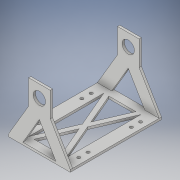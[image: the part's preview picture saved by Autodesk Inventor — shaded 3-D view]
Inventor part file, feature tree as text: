
AUTODESK INVENTOR PART (.ipt)
format: ipt  version: 2019 (Build 230136000, 136)  size: 211,968 bytes
history: native  units: in
note: dims shown in document units (in); Inventor stores cm internally (conversion verified against a paired STEP export)
features: sketch x7, extrude x6, plane x2, mirror x2
ambient origin geometry x8: Origin, YZ Plane, XZ Plane, XY Plane, X Axis, Y Axis, Z Axis, Center Point
bodies: Body1 (feature_tree)
feature tree (17):
  extrude  "Extrusion3"  TaperAngle=0.0deg  [1 undecoded]
  extrude  "Extrusion4"  Depth=3.5in
  sketch  "Sketch8"  dims[d56=2.0in d57=2.0in]
  plane  "Work Plane2"
  mirror  "Mirror3"
  extrude  "Extrusion8"  Depth=2.0in
  mirror  "Mirror4"
  extrude  "Extrusion9"  Depth=1.0in TaperAngle=0.0deg
  extrude  "Extrusion10"  Depth=0.375in TaperAngle=0.0deg
  extrude  "Extrusion11"  [1 undecoded]
  sketch  "Sketch1"  dims[d22=0.375in d23=0.0in d31=0.0in d32=0.0in]
  sketch  "Sketch7"  dims[d33=7.0in d52=3.5in]
  plane  "Work Plane3"
  sketch  "Sketch13"  dims[d58=0.375in d59=0.0in d60=1.0in d61=0.0in]
  sketch  "Sketch14"  dims[d75=0.375in d76=0.0in d77=0.375in d78=0.0in]
  sketch  "Sketch15"
  sketch  "Sketch16"
note: 2 required parameter values undecoded (feature->parameter linkage not recoverable at this tier; creation-order binding heuristic only, values carry confidence <= 0.55)
